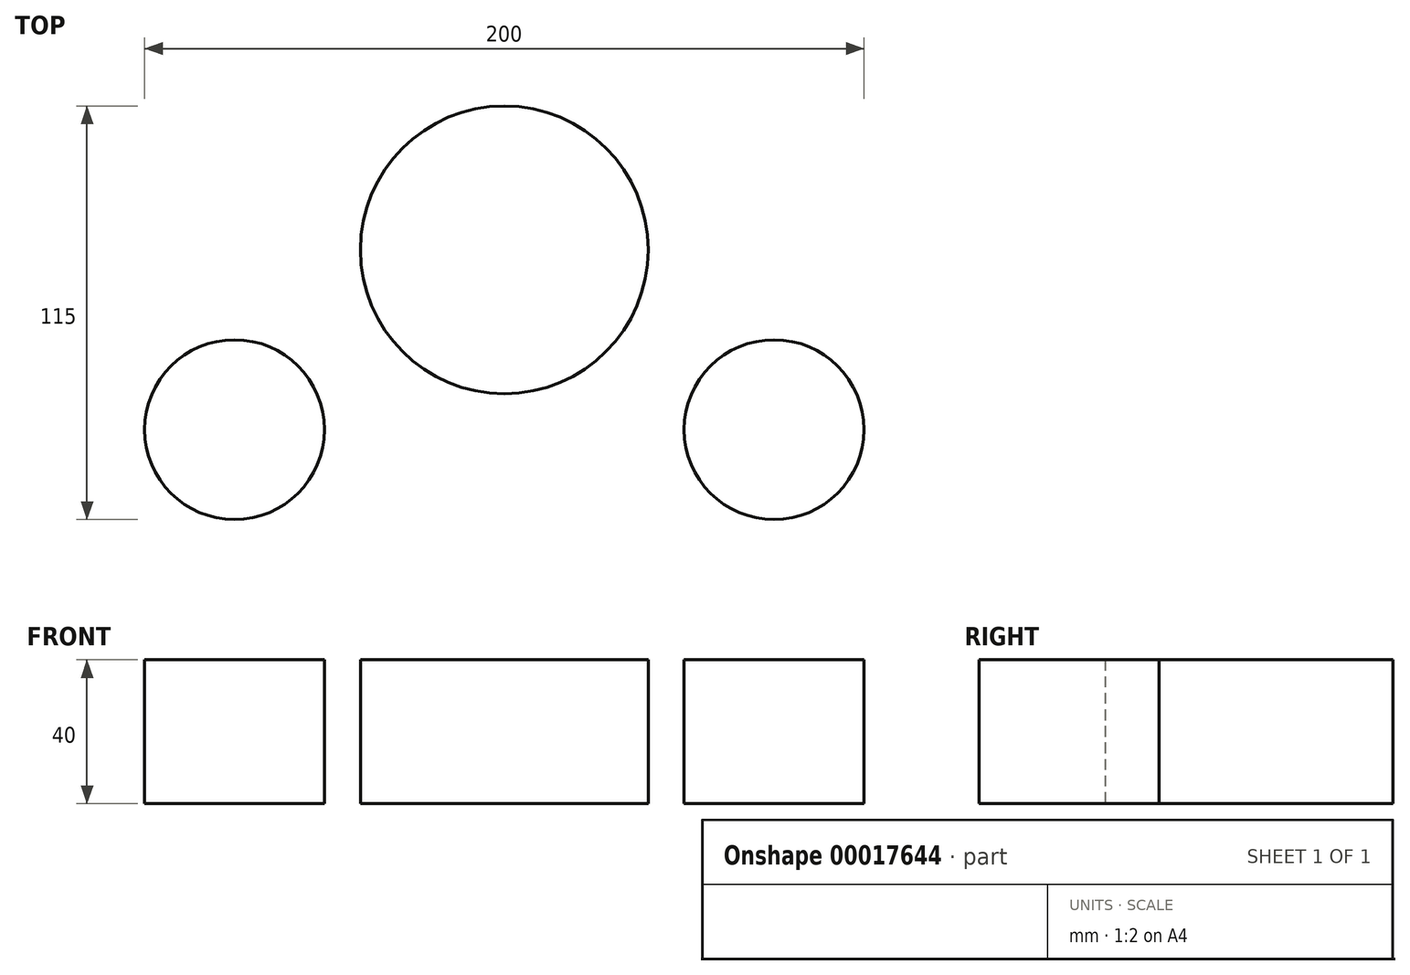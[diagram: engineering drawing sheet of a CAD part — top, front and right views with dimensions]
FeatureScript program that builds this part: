
annotation { "Feature Type Name" : "Feature", "Feature Type Description" : "" }
export const myFeature = defineFeature(function(context is Context, id is Id, definition is map)
    precondition{}
    {
        {
            var Q0;
            Q0=qCreatedBy(makeId("Top.planeOp"),FACE);
            var sketch = newSketch(context, id + "F0", { "sketchPlane" : qUnion([Q0])});
            skCircle(sketch, "E0", {"center": v(-75, 0) * mm, "radius": 25 * mm});
            skCircle(sketch, "E1", {"center": v(75, 0) * mm, "radius": 25 * mm});
            skCircle(sketch, "E2", {"center": v(0, 50) * mm, "radius": 40 * mm});
            skLineSegment(sketch, "E3", {"start": v(-75, -25) * mm, "end": v(75, -25) * mm});
            skLineSegment(sketch, "E4", {"start": v(-75, 25) * mm, "end": v(75, 25) * mm});
            skLineSegment(sketch, "E5", {"start": v(-92.14, 18.2) * mm, "end": v(-27.42, 79.13) * mm});
            skLineSegment(sketch, "E6", {"start": v(92.14, 18.2) * mm, "end": v(27.42, 79.13) * mm});
            skSolve(sketch);
        }
        {
            var Q0;
            {var subQ0=sQuery(id+"F0.wireOp",EDGE,"E0");var subQ1=makeQuery(id+"F0.imprint","INTERSECT",VERTEX,{"derivedFrom":[subQ0,sQuery(id+"F0.wireOp",EDGE,"E4")]});Q0=makeQuery(id+"F0.imprint","IMPRINT",FACE,{"disambiguationData":[TD([[makeQuery(id+"F0.imprint","IMPRINT",EDGE,{"disambiguationData":[TD([[subQ1,-1.0]])],"derivedFrom":subQ0}),1.0]])]});}
            var Q1;
            {var subQ1=sQuery(id+"F0.wireOp",EDGE,"E2");var subQ5=makeQuery(id+"F0.imprint","INTERSECT",VERTEX,{"derivedFrom":[subQ1,sQuery(id+"F0.wireOp",EDGE,"E5")]});Q1=makeQuery(id+"F0.imprint","IMPRINT",FACE,{"disambiguationData":[TD([[makeQuery(id+"F0.imprint","IMPRINT",EDGE,{"disambiguationData":[TD([[subQ5,1.0]])],"derivedFrom":subQ1}),1.0]])]});}
            var Q2;
            {var subQ0=sQuery(id+"F0.wireOp",EDGE,"E4");var subQ1=sQuery(id+"F0.wireOp",EDGE,"E2");var subQ3=makeQuery(id+"F0.imprint","INTERSECT",VERTEX,{"disambiguationData":[OD(0.0)],"derivedFrom":[subQ1,subQ0]});Q2=makeQuery(id+"F0.imprint","IMPRINT",FACE,{"disambiguationData":[TD([[makeQuery(id+"F0.imprint","IMPRINT",EDGE,{"disambiguationData":[TD([[subQ3,-1.0]])],"derivedFrom":subQ1}),1.0]])]});}
            var Q3;
            {var subQ0=sQuery(id+"F0.wireOp",EDGE,"E1");var subQ3=makeQuery(id+"F0.imprint","INTERSECT",VERTEX,{"derivedFrom":[subQ0,sQuery(id+"F0.wireOp",EDGE,"E4")]});Q3=makeQuery(id+"F0.imprint","IMPRINT",FACE,{"disambiguationData":[TD([[makeQuery(id+"F0.imprint","IMPRINT",EDGE,{"disambiguationData":[TD([[subQ3,1.0]])],"derivedFrom":subQ0}),1.0]])]});}
            extrude(context, id + "F1", {"entities" : qUnion([Q0, Q1, Q2, Q3]), "depth" : 40 * mm});
        }
    });
